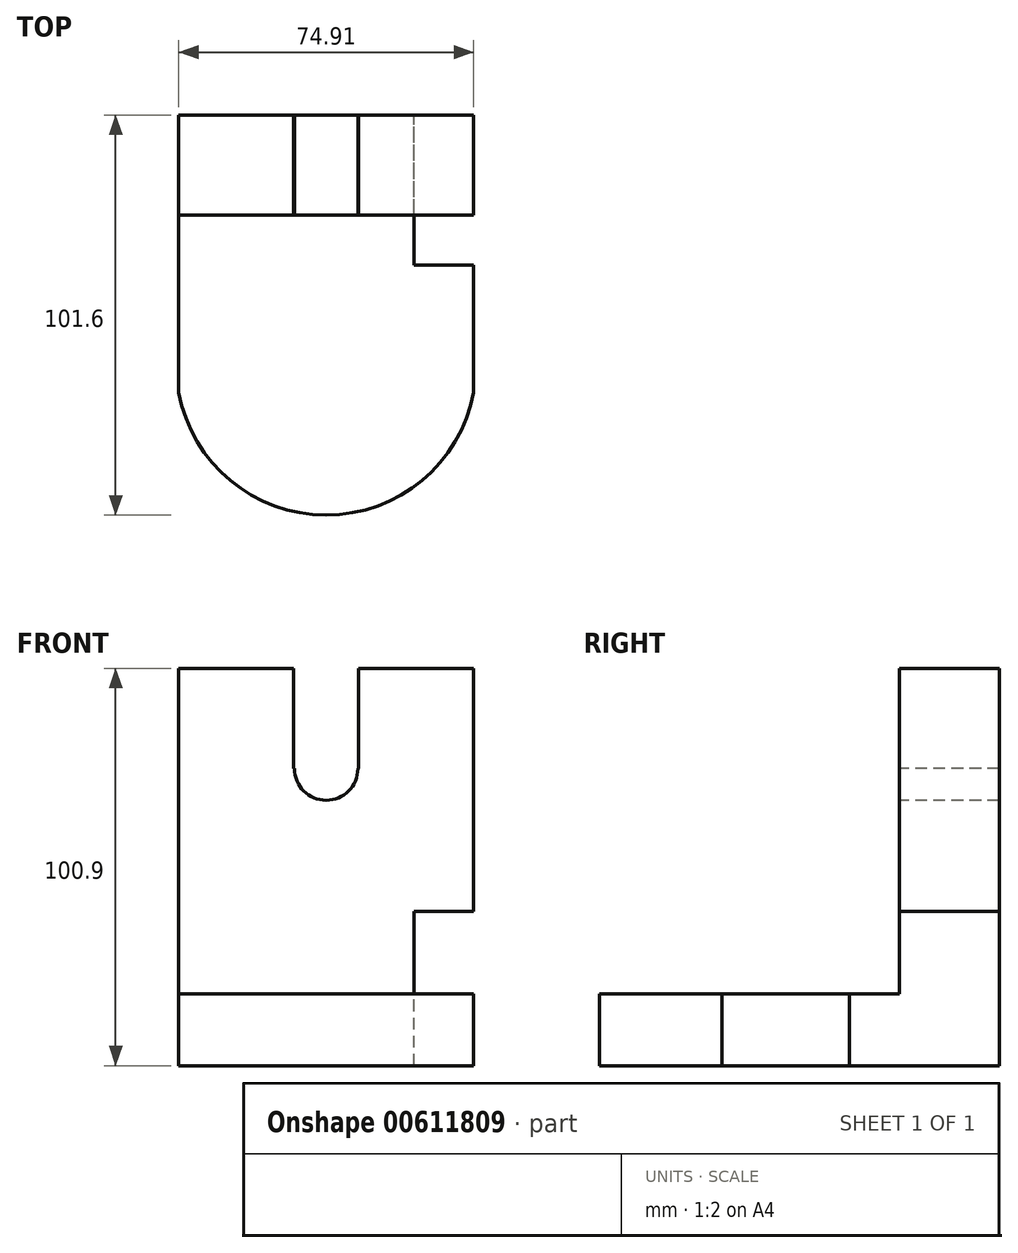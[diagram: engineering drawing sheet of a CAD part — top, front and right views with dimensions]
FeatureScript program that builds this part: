
annotation { "Feature Type Name" : "Feature", "Feature Type Description" : "" }
export const myFeature = defineFeature(function(context is Context, id is Id, definition is map)
    precondition{}
    {
        {
            var Q0;
            Q0=qCreatedBy(makeId("Front.planeOp"),FACE);
            var sketch = newSketch(context, id + "F0", { "sketchPlane" : qUnion([Q0])});
            skLineSegment(sketch, "E0.bottom", {"start": v(-37.46, 61.74) * mm, "end": v(37.45, 61.74) * mm});
            skLineSegment(sketch, "E0.top", {"start": v(-37.46, -27.53) * mm, "end": v(37.45, -27.53) * mm});
            skLineSegment(sketch, "E0.left", {"start": v(-37.46, 61.74) * mm, "end": v(-37.46, -27.53) * mm});
            skLineSegment(sketch, "E0.right", {"start": v(37.45, 61.74) * mm, "end": v(37.45, -27.53) * mm});
            skLineSegment(sketch, "E1.top", {"start": v(-37.46, -39.16) * mm, "end": v(37.45, -39.16) * mm});
            skLineSegment(sketch, "E1.left", {"start": v(-37.46, -27.53) * mm, "end": v(-37.46, -39.16) * mm});
            skLineSegment(sketch, "E1.right", {"start": v(37.45, -27.53) * mm, "end": v(37.45, -39.16) * mm});
            skSolve(sketch);
        }
        {
            var Q0;
            Q0 = qSketchRegion(id + "F0", true);
            extrude(context, id + "F1", {"entities" : qUnion([Q0]), "depth" : 25.4 * mm, "offsetDistance" : 25.4 * mm});
        }
        {
            var Q0;
            Q0=makeQuery(id+"F1.opExtrude","CAP_FACE",FACE,{"disambiguationData":[OSD([sQuery(id+"F0.wireOp",EDGE,"E0.bottom"),sQuery(id+"F0.wireOp",EDGE,"E0.left"),sQuery(id+"F0.wireOp",EDGE,"E0.right"),sQuery(id+"F0.wireOp",EDGE,"E1.top"),sQuery(id+"F0.wireOp",EDGE,"E1.left"),sQuery(id+"F0.wireOp",EDGE,"E1.right")])],"isStart":false});
            var sketch = newSketch(context, id + "F2", { "sketchPlane" : qUnion([Q0])});
            skLineSegment(sketch, "E2.bottom", {"start": v(8.24, 36.3) * mm, "end": v(-8.24, 36.3) * mm});
            skLineSegment(sketch, "E2.top", {"start": v(8.24, 87.17) * mm, "end": v(-8.24, 87.17) * mm});
            skLineSegment(sketch, "E2.left", {"start": v(8.24, 36.3) * mm, "end": v(8.24, 87.17) * mm});
            skLineSegment(sketch, "E2.right", {"start": v(-8.24, 36.3) * mm, "end": v(-8.24, 87.17) * mm});
            skPoint(sketch, "E2.middle", {"position": v(0, 61.74) * mm});
            skCircle(sketch, "E3", {"center": v(0, 36.3) * mm, "radius": 8.05 * mm});
            skSolve(sketch);
        }
        {
            var Q0;
            Q0 = qSketchRegion(id + "F2", true);
            extrude(context, id + "F3", {"entities" : qUnion([Q0]), "operationType" : NewBodyOperationType.REMOVE, "endBound" : BoundingType.SYMMETRIC, "oppositeDirection" : true, "depth" : 76.2 * mm, "offsetDistance" : 25.4 * mm});
        }
        {
            var Q0;
            Q0=makeQuery(id+"F1.opExtrude","CAP_FACE",FACE,{"disambiguationData":[OSD([sQuery(id+"F0.wireOp",EDGE,"E0.bottom"),sQuery(id+"F0.wireOp",EDGE,"E0.left"),sQuery(id+"F0.wireOp",EDGE,"E0.right"),sQuery(id+"F0.wireOp",EDGE,"E1.top"),sQuery(id+"F0.wireOp",EDGE,"E1.left"),sQuery(id+"F0.wireOp",EDGE,"E1.right")])],"isStart":false});
            var sketch = newSketch(context, id + "F4", { "sketchPlane" : qUnion([Q0])});
            skLineSegment(sketch, "E4.bottom", {"start": v(-37.46, -39.16) * mm, "end": v(37.45, -39.16) * mm});
            skLineSegment(sketch, "E4.top", {"start": v(-37.46, -20.94) * mm, "end": v(37.45, -20.94) * mm});
            skLineSegment(sketch, "E4.left", {"start": v(-37.46, -39.16) * mm, "end": v(-37.46, -20.94) * mm});
            skLineSegment(sketch, "E4.right", {"start": v(37.45, -39.16) * mm, "end": v(37.45, -20.94) * mm});
            skSolve(sketch);
        }
        {
            var Q0;
            Q0 = qSketchRegion(id + "F4", true);
            extrude(context, id + "F5", {"entities" : qUnion([Q0]), "operationType" : NewBodyOperationType.ADD, "depth" : 76.2 * mm, "offsetDistance" : 25.4 * mm});
        }
        {
            var Q0;
            Q0=makeQuery(id+"F5.opExtrude","SWEPT_FACE",FACE,{"disambiguationData":[OSD([sQuery(id+"F4.wireOp",EDGE,"E4.top")])]});
            var sketch = newSketch(context, id + "F6", { "sketchPlane" : qUnion([Q0])});
            skLineSegment(sketch, "E5.bottom", {"start": v(-37.46, -25.4) * mm, "end": v(37.45, -25.4) * mm});
            skLineSegment(sketch, "E5.top", {"start": v(-37.46, -63.5) * mm, "end": v(37.45, -63.5) * mm});
            skLineSegment(sketch, "E5.left", {"start": v(-37.46, -25.4) * mm, "end": v(-37.46, -63.5) * mm});
            skLineSegment(sketch, "E5.right", {"start": v(37.45, -25.4) * mm, "end": v(37.45, -63.5) * mm});
            skCircle(sketch, "E6", {"center": v(0, -63.5) * mm, "radius": 38.1 * mm});
            skLineSegment(sketch, "E7.top", {"start": v(-37.46, -101.6) * mm, "end": v(37.45, -101.6) * mm});
            skLineSegment(sketch, "E7.left", {"start": v(-37.46, -63.5) * mm, "end": v(-37.46, -101.6) * mm});
            skLineSegment(sketch, "E7.right", {"start": v(37.45, -63.5) * mm, "end": v(37.45, -101.6) * mm});
            skSolve(sketch);
        }
        {
            var Q0;
            {var subQ0=sQuery(id+"F6.wireOp",EDGE,"E7.left");var subQ1=sQuery(id+"F6.wireOp",EDGE,"E6");var subQ2=makeQuery(id+"F6.imprint","INTERSECT",VERTEX,{"derivedFrom":[subQ1,subQ0]});Q0=makeQuery(id+"F6.imprint","IMPRINT",FACE,{"disambiguationData":[TD([[makeQuery(id+"F6.imprint","IMPRINT",EDGE,{"disambiguationData":[TD([[subQ2,-1.0]])],"derivedFrom":subQ1}),-1.0]])]});}
            var Q1;
            {var subQ0=sQuery(id+"F6.wireOp",EDGE,"E7.top");var subQ1=sQuery(id+"F6.wireOp",EDGE,"E6");var subQ2=makeQuery(id+"F6.imprint","INTERSECT",VERTEX,{"derivedFrom":[subQ1,subQ0]});Q1=makeQuery(id+"F6.imprint","IMPRINT",FACE,{"disambiguationData":[TD([[makeQuery(id+"F6.imprint","IMPRINT",EDGE,{"disambiguationData":[TD([[subQ2,-1.0]])],"derivedFrom":subQ1}),-1.0]])]});}
            extrude(context, id + "F7", {"entities" : qUnion([Q0, Q1]), "operationType" : NewBodyOperationType.REMOVE, "oppositeDirection" : true, "depth" : 25.4 * mm, "offsetDistance" : 25.4 * mm});
        }
        {
            var Q0;
            Q0=makeQuery(id+"F1.opExtrude","CAP_FACE",FACE,{"disambiguationData":[OSD([sQuery(id+"F0.wireOp",EDGE,"E0.bottom"),sQuery(id+"F0.wireOp",EDGE,"E0.left"),sQuery(id+"F0.wireOp",EDGE,"E0.right"),sQuery(id+"F0.wireOp",EDGE,"E1.top"),sQuery(id+"F0.wireOp",EDGE,"E1.left"),sQuery(id+"F0.wireOp",EDGE,"E1.right")])],"isStart":true});
            var sketch = newSketch(context, id + "F8", { "sketchPlane" : qUnion([Q0])});
            skLineSegment(sketch, "E8.bottom", {"start": v(-37.45, -39.16) * mm, "end": v(-22.33, -39.16) * mm});
            skLineSegment(sketch, "E8.top", {"start": v(-37.45, 0) * mm, "end": v(-22.33, 0) * mm});
            skLineSegment(sketch, "E8.left", {"start": v(-37.45, -39.16) * mm, "end": v(-37.45, 0) * mm});
            skLineSegment(sketch, "E8.right", {"start": v(-22.33, -39.16) * mm, "end": v(-22.33, 0) * mm});
            skSolve(sketch);
        }
        {
            var Q0;
            Q0 = qSketchRegion(id + "F8", true);
            extrude(context, id + "F9", {"entities" : qUnion([Q0]), "operationType" : NewBodyOperationType.REMOVE, "oppositeDirection" : true, "depth" : 38.1 * mm, "offsetDistance" : 25.4 * mm});
        }
    });
